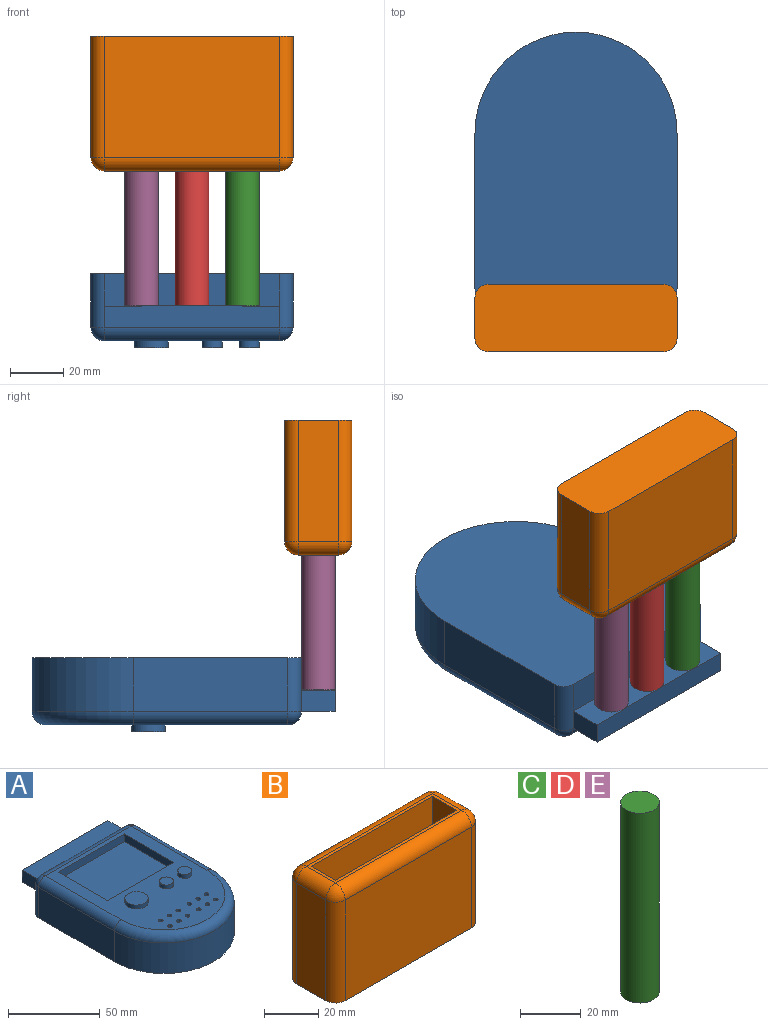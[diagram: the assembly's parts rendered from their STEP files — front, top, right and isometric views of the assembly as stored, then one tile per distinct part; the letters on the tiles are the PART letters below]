
ASSEMBLY  parts=5 mates=4
PART A: 58 faces, bbox 82.5x117.4x27.9 mm
  f0: plane 13.97x12.7mm, normal (0,0,-1), area 177.4mm2, adj f1,f52,f54,f55
  f1: plane 66.04x12.39mm, normal (0,1,0), area 808.7mm2, adj f0,f6,f42,f44,f51,f55,f56,f57
  f2: plane 91.44x66.04mm, normal (0,0,1), area 3356.6mm2, adj f7,f8,f9,f10,f12,f14,f16,f18
  f3: plane 58.42x20.32mm, normal (-1,0,0), area 1187.1mm2, adj f4,f6,f44,f49
  f4: cylinder r=38.1mm len=76.2mm, axis (0,0,-1), area 2432.2mm2, adj f3,f5,f6,f48
  f5: plane 58.42x20.32mm, normal (1,0,0), area 1187.1mm2, adj f4,f6,f42,f46
  f6: plane 101.6x76.2mm, normal (0,0,-1), area 7107.8mm2, adj f1,f3,f4,f5,f42,f44
  f7: plane 50.8x5.08mm, normal (0,-1,0), area 258.1mm2, adj f2,f8,f10,f11
  f8: plane 38.1x5.08mm, normal (1,0,0), area 193.5mm2, adj f2,f7,f9,f11
  f9: plane 50.8x5.08mm, normal (0,1,0), area 258.1mm2, adj f2,f8,f10,f11
  f10: plane 38.1x5.08mm, normal (-1,0,0), area 193.5mm2, adj f2,f7,f9,f11
  f11: plane 50.8x38.1mm, normal (0,0,1), area 1935.5mm2, adj f7,f8,f9,f10
  f12: cylinder r=6.35mm len=12.7mm, axis (0,0,-1), area 101.3mm2, adj f2,f13
  f13: plane 12.7x12.7mm, normal (0,0,1), area 126.7mm2, adj f12
  f14: cylinder r=3.81mm len=7.62mm, axis (0,0,-1), area 60.8mm2, adj f2,f15
  f15: plane 7.62x7.62mm, normal (0,0,1), area 45.6mm2, adj f14
  f16: cylinder r=3.81mm len=7.62mm, axis (0,0,-1), area 60.8mm2, adj f2,f17
  f17: plane 7.62x7.62mm, normal (0,0,1), area 45.6mm2, adj f16
  f18: cylinder r=1.27mm len=7.62mm, axis (0,0,1), area 60.8mm2, adj f2,f19
  f19: plane 2.54x2.54mm, normal (0,0,1), area 5.1mm2, adj f18
  f20: cylinder r=1.27mm len=7.62mm, axis (0,0,1), area 60.8mm2, adj f2,f21
  f21: plane 2.54x2.54mm, normal (0,0,1), area 5.1mm2, adj f20
  f22: cylinder r=1.27mm len=7.62mm, axis (0,0,1), area 60.8mm2, adj f2,f23
  f23: plane 2.54x2.54mm, normal (0,0,1), area 5.1mm2, adj f22
  f24: cylinder r=1.27mm len=7.62mm, axis (0,0,1), area 60.8mm2, adj f2,f25
  f25: plane 2.54x2.54mm, normal (0,0,1), area 5.1mm2, adj f24
  f26: cylinder r=1.27mm len=7.62mm, axis (0,0,1), area 60.8mm2, adj f2,f27
  f27: plane 2.54x2.54mm, normal (0,0,1), area 5.1mm2, adj f26
  f28: cylinder r=1.27mm len=7.62mm, axis (0,0,1), area 60.8mm2, adj f2,f29
  f29: plane 2.54x2.54mm, normal (0,0,1), area 5.1mm2, adj f28
  f30: cylinder r=1.27mm len=7.62mm, axis (0,0,1), area 60.8mm2, adj f2,f31
  f31: plane 2.54x2.54mm, normal (0,0,1), area 5.1mm2, adj f30
  f32: cylinder r=1.27mm len=7.62mm, axis (0,0,1), area 60.8mm2, adj f2,f33
  f33: plane 2.54x2.54mm, normal (0,0,1), area 5.1mm2, adj f32
  f34: cylinder r=1.27mm len=7.62mm, axis (0,0,1), area 60.8mm2, adj f2,f35
  f35: plane 2.54x2.54mm, normal (0,0,1), area 5.1mm2, adj f34
  f36: cylinder r=1.27mm len=7.62mm, axis (0,0,1), area 60.8mm2, adj f2,f37
  f37: plane 2.54x2.54mm, normal (0,0,1), area 5.1mm2, adj f36
  f38: cylinder r=1.27mm len=7.62mm, axis (0,0,1), area 60.8mm2, adj f2,f39
  f39: plane 2.54x2.54mm, normal (0,0,1), area 5.1mm2, adj f38
  f40: cylinder r=1.27mm len=7.62mm, axis (0,0,1), area 60.8mm2, adj f2,f41
  f41: plane 2.54x2.54mm, normal (0,0,1), area 5.1mm2, adj f40
  f42: cylinder r=5.08mm len=20.32mm, axis (0,0,-1), area 162.1mm2, adj f1,f5,f6,f43,f50
  f43: sphere r=5.08mm, area 40.5mm2, adj f42,f45,f46
  f44: cylinder r=5.08mm len=20.32mm, axis (0,0,1), area 162.1mm2, adj f1,f3,f6,f47,f52
  f45: cylinder r=5.08mm len=66.04mm, axis (1,0,0), area 527mm2, adj f2,f43,f47,f53
  f46: cylinder r=5.08mm len=58.42mm, axis (0,-1,0), area 466.2mm2, adj f2,f5,f43,f48
  f47: sphere r=5.08mm, area 40.5mm2, adj f44,f45,f49
  f48: torus R=33.02mm, axis (0,0,1), area 908.8mm2, adj f2,f4,f46,f49
  f49: cylinder r=5.08mm len=58.42mm, axis (0,1,0), area 466.2mm2, adj f2,f3,f47,f48
  f50: plane 12.7x7.93mm, normal (1,0,0), area 100.7mm2, adj f42,f51,f53,f54
  f51: plane 13.97x12.7mm, normal (0,0,-1), area 177.4mm2, adj f1,f50,f54,f56
  f52: plane 12.7x7.93mm, normal (-1,0,0), area 100.7mm2, adj f0,f44,f53,f54
  f53: plane 66.04x12.7mm, normal (0,0,1), area 838.7mm2, adj f45,f50,f52,f54
  f54: plane 66.04x8.18mm, normal (0,1,0), area 533.3mm2, adj f0,f50,f51,f52,f53,f55,f56,f57
  f55: plane 12.7x0.25mm, normal (-1,0,0), area 3.2mm2, adj f0,f1,f54,f57
  f56: plane 12.7x0.25mm, normal (1,0,0), area 3.2mm2, adj f1,f51,f54,f57
  f57: plane 38.1x12.7mm, normal (0,0,-1), area 483.9mm2, adj f1,f54,f55,f56
PART B: 23 faces, bbox 76.2x25.4x50.8 mm
  f0: plane 66.04x15.24mm, normal (0,0,1), area 200mm2, adj f6,f7,f8,f9,f14,f15,f19,f20
  f1: plane 66.04x45.72mm, normal (0,1,0), area 3019.3mm2, adj f5,f13,f19,f22
  f2: plane 45.72x15.24mm, normal (-1,0,0), area 696.8mm2, adj f5,f16,f20,f22
  f3: plane 66.04x45.72mm, normal (0,-1,0), area 3019.3mm2, adj f5,f11,f15,f16
  f4: plane 45.72x15.24mm, normal (1,0,0), area 696.8mm2, adj f5,f11,f13,f14
  f5: plane 76.2x25.4mm, normal (0,0,-1), area 1913.3mm2, adj f1,f2,f3,f4,f11,f13,f16,f22
  f6: plane 63.5x25.4mm, normal (0,-1,0), area 1612.9mm2, adj f0,f7,f9,f10
  f7: plane 25.4x12.7mm, normal (1,0,0), area 322.6mm2, adj f0,f6,f8,f10
  f8: plane 63.5x25.4mm, normal (0,1,0), area 1612.9mm2, adj f0,f7,f9,f10
  f9: plane 25.4x12.7mm, normal (-1,0,0), area 322.6mm2, adj f0,f6,f8,f10
  f10: plane 63.5x12.7mm, normal (0,0,1), area 806.5mm2, adj f6,f7,f8,f9
  f11: cylinder r=5.08mm len=45.72mm, axis (0,0,-1), area 364.8mm2, adj f3,f4,f5,f12
  f12: sphere r=5.08mm, area 40.5mm2, adj f11,f14,f15
  f13: cylinder r=5.08mm len=45.72mm, axis (0,0,1), area 364.8mm2, adj f1,f4,f5,f17
  f14: cylinder r=5.08mm len=15.24mm, axis (0,1,0), area 121.6mm2, adj f0,f4,f12,f17
  f15: cylinder r=5.08mm len=66.04mm, axis (1,0,0), area 527mm2, adj f0,f3,f12,f18
  f16: cylinder r=5.08mm len=45.72mm, axis (0,0,1), area 364.8mm2, adj f2,f3,f5,f18
  f17: sphere r=5.08mm, area 40.5mm2, adj f13,f14,f19
  f18: sphere r=5.08mm, area 40.5mm2, adj f15,f16,f20
  f19: cylinder r=5.08mm len=66.04mm, axis (-1,0,0), area 527mm2, adj f0,f1,f17,f21
  f20: cylinder r=5.08mm len=15.24mm, axis (0,-1,0), area 121.6mm2, adj f0,f2,f18,f21
  f21: sphere r=5.08mm, area 40.5mm2, adj f19,f20,f22
  f22: cylinder r=5.08mm len=45.72mm, axis (0,0,-1), area 364.8mm2, adj f1,f2,f5,f21
PART C: 3 faces, bbox 12.7x12.7x76.2 mm
  f0: cylinder r=6.35mm len=76.2mm, axis (0,0,-1), area 3040.2mm2, adj f1,f2
  f1: plane 12.7x12.7mm, normal (0,0,1), area 126.7mm2, adj f0
  f2: plane 12.7x12.7mm, normal (0,0,-1), area 126.7mm2, adj f0
PART D: same geometry as C
PART E: same geometry as C
PLACE A rot(axis=(1,0,0),180deg) t=(-38.6,-32.62,9.91)mm
PLACE B rot(axis=(1,0,0),180deg) t=(0.47,-59.37,48.57)mm
PLACE C t=(37.7,-5.51,-2.23)mm
PLACE D t=(18.65,-5.51,-2.23)mm
PLACE E t=(-0.4,-5.51,-2.23)mm
MATE fastened A.f57 <-> E.f0  axis (0,0,1) through (-55.69,-60.32,-2.23)mm
MATE fastened A.f57 <-> C.f0  axis (0,0,1) through (-17.59,-60.32,-2.23)mm
MATE fastened D.f0 <-> A.f57  axis (0,0,-1) through (-36.64,-60.32,-2.23)mm
MATE fastened D.f0 <-> B.f10  axis (0,0,1) through (-36.64,-60.32,73.97)mm
